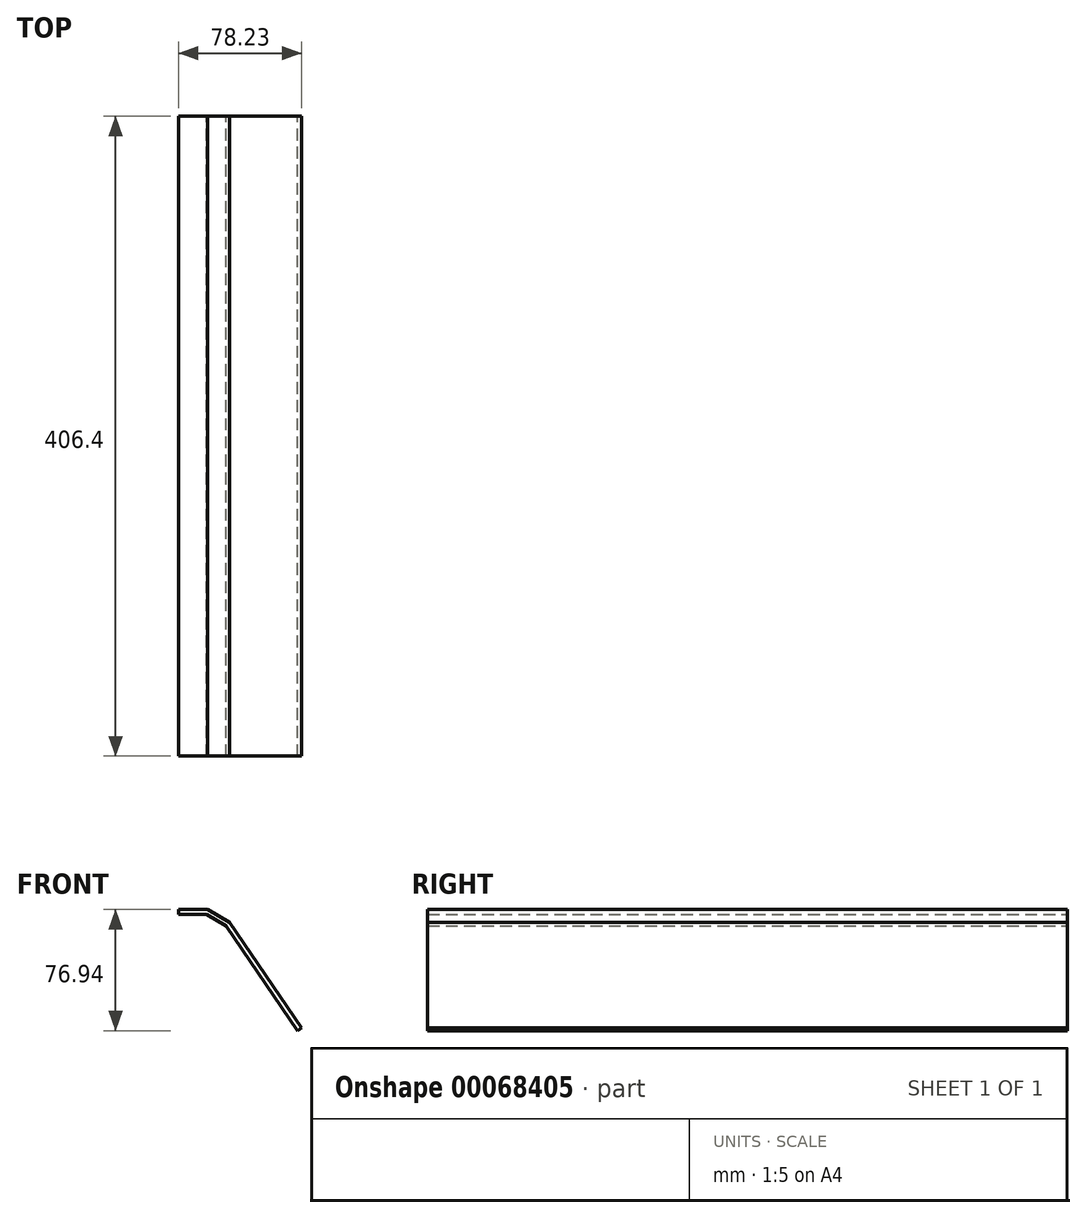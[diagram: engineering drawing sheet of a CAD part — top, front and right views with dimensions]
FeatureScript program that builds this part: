
annotation { "Feature Type Name" : "Feature", "Feature Type Description" : "" }
export const myFeature = defineFeature(function(context is Context, id is Id, definition is map)
    precondition{}
    {
        {
            var Q0;
            Q0=qCreatedBy(makeId("Front.planeOp"),FACE);
            var sketch = newSketch(context, id + "F0", { "sketchPlane" : qUnion([Q0])});
            skLineSegment(sketch, "E0", {"start": v(0, 0) * mm, "end": v(18.45, 0) * mm});
            skLineSegment(sketch, "E1", {"start": v(0, 0) * mm, "end": v(0, -3.17) * mm});
            skLineSegment(sketch, "E2", {"start": v(0, -3.17) * mm, "end": v(17.6, -3.17) * mm});
            skLineSegment(sketch, "E3", {"start": v(17.6, -3.17) * mm, "end": v(30.12, -10.4) * mm});
            skLineSegment(sketch, "E4", {"start": v(30.12, -10.4) * mm, "end": v(75.6, -76.94) * mm});
            skLineSegment(sketch, "E5", {"start": v(75.6, -76.94) * mm, "end": v(78.23, -75.14) * mm});
            skLineSegment(sketch, "E6", {"start": v(32.33, -8.01) * mm, "end": v(78.23, -75.14) * mm});
            skLineSegment(sketch, "E7", {"start": v(32.33, -8.01) * mm, "end": v(18.45, 0) * mm});
            skPoint(sketch, "E8", {"position": v(37.93, -14.9) * mm});
            skSolve(sketch);
        }
        {
            var Q0;
            Q0 = qSketchRegion(id + "F0", true);
            extrude(context, id + "F1", {"entities" : qUnion([Q0]), "depth" : 406.4 * mm});
        }
    });
